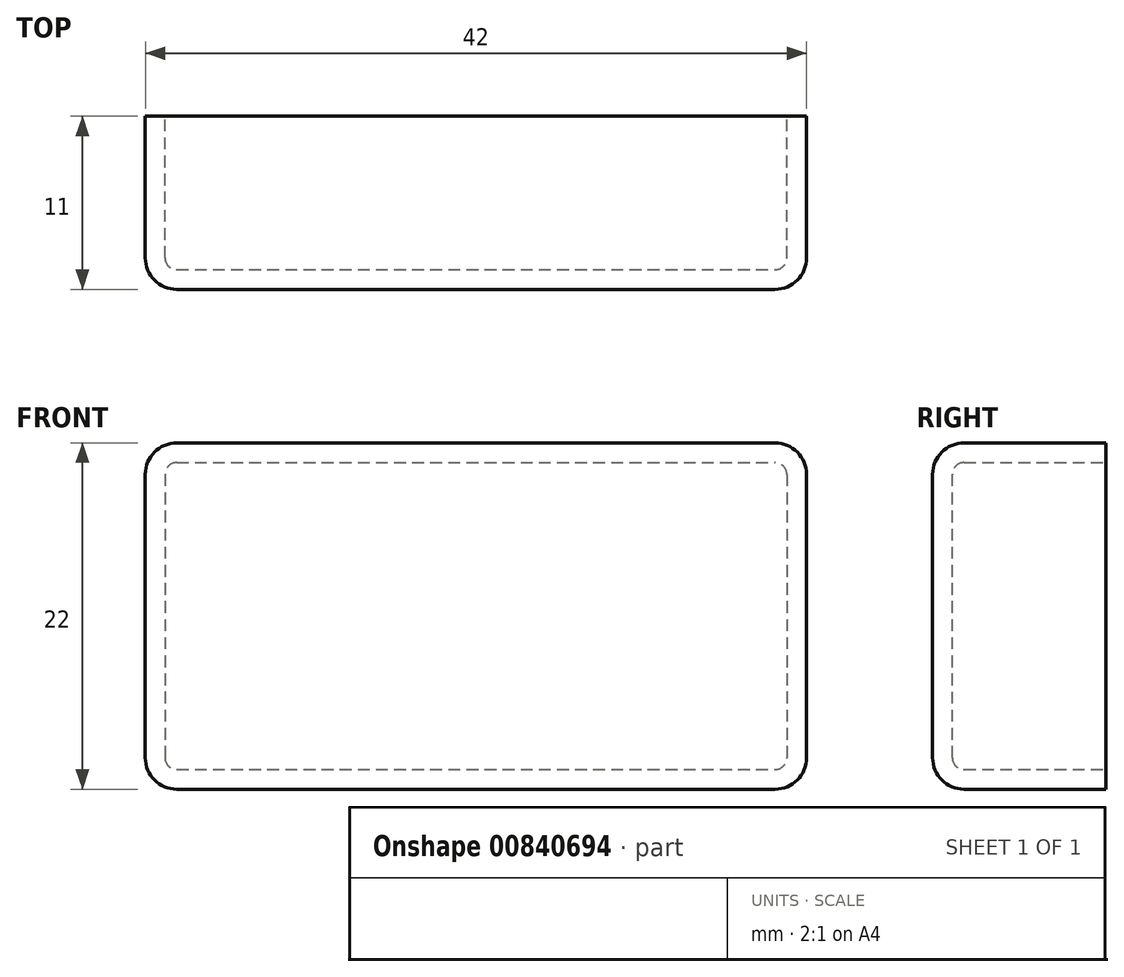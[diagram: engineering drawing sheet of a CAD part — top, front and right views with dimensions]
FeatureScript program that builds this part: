
annotation { "Feature Type Name" : "Feature", "Feature Type Description" : "" }
export const myFeature = defineFeature(function(context is Context, id is Id, definition is map)
    precondition{}
    {
        {
            var Q0;
            Q0=qCreatedBy(makeId("Front.planeOp"),FACE);
            var sketch = newSketch(context, id + "F0", { "sketchPlane" : qUnion([Q0])});
            skLineSegment(sketch, "E0.bottom", {"start": v(-16.62, 8.33) * mm, "end": v(25.38, 8.33) * mm});
            skLineSegment(sketch, "E0.top", {"start": v(-16.62, -13.67) * mm, "end": v(25.38, -13.67) * mm});
            skLineSegment(sketch, "E0.left", {"start": v(-16.62, 8.33) * mm, "end": v(-16.62, -13.67) * mm});
            skLineSegment(sketch, "E0.right", {"start": v(25.38, 8.33) * mm, "end": v(25.38, -13.67) * mm});
            skSolve(sketch);
        }
        {
            var Q0;
            Q0=makeQuery(id+"F0.imprint","IMPRINT",FACE,{"disambiguationData":[TD([[makeQuery(id+"F0.imprint","IMPRINT",EDGE,{"derivedFrom":sQuery(id+"F0.wireOp",EDGE,"E0.bottom")}),-1.0]])]});
            extrude(context, id + "F1", {"entities" : qUnion([Q0]), "depth" : 11 * mm, "offsetDistance" : 25 * mm});
        }
        {
            var Q0;
            Q0=makeQuery(id+"F1.opExtrude","SWEPT_EDGE",EDGE,{"disambiguationData":[OSD([sQuery(id+"F0.wireOp",EDGE,"E0.bottom"),sQuery(id+"F0.wireOp",EDGE,"E0.right")])]});
            var Q1;
            Q1=makeQuery(id+"F1.opExtrude","SWEPT_EDGE",EDGE,{"disambiguationData":[OSD([sQuery(id+"F0.wireOp",EDGE,"E0.top"),sQuery(id+"F0.wireOp",EDGE,"E0.right")])]});
            var Q2;
            Q2=makeQuery(id+"F1.opExtrude","SWEPT_EDGE",EDGE,{"disambiguationData":[OSD([sQuery(id+"F0.wireOp",EDGE,"E0.bottom"),sQuery(id+"F0.wireOp",EDGE,"E0.left")])]});
            var Q3;
            Q3=makeQuery(id+"F1.opExtrude","SWEPT_EDGE",EDGE,{"disambiguationData":[OSD([sQuery(id+"F0.wireOp",EDGE,"E0.top"),sQuery(id+"F0.wireOp",EDGE,"E0.left")])]});
            var Q4;
            Q4=makeQuery(id+"F1.opExtrude","CAP_EDGE",EDGE,{"disambiguationData":[OSD([sQuery(id+"F0.wireOp",EDGE,"E0.top")])],"isStart":false});
            var Q5;
            Q5=makeQuery(id+"F1.opExtrude","CAP_EDGE",EDGE,{"disambiguationData":[OSD([sQuery(id+"F0.wireOp",EDGE,"E0.right")])],"isStart":false});
            var Q6;
            Q6=makeQuery(id+"F1.opExtrude","CAP_EDGE",EDGE,{"disambiguationData":[OSD([sQuery(id+"F0.wireOp",EDGE,"E0.bottom")])],"isStart":false});
            var Q7;
            Q7=makeQuery(id+"F1.opExtrude","CAP_EDGE",EDGE,{"disambiguationData":[OSD([sQuery(id+"F0.wireOp",EDGE,"E0.left")])],"isStart":false});
            fillet(context, id + "F2", {"entities" : qUnion([Q0, Q1, Q2, Q3, Q4, Q5, Q6, Q7]), "radius" : 2 * mm, "tangentPropagation" : true, "allowEdgeOverflow" : false});
        }
        {
            var Q0;
            Q0=makeQuery(id+"F1.opExtrude","CAP_FACE",FACE,{"disambiguationData":[OSD([sQuery(id+"F0.wireOp",EDGE,"E0.bottom"),sQuery(id+"F0.wireOp",EDGE,"E0.top"),sQuery(id+"F0.wireOp",EDGE,"E0.left"),sQuery(id+"F0.wireOp",EDGE,"E0.right")])],"isStart":true});
            shell(context, id + "F3", {"entities" : qUnion([Q0]), "thickness" : 1.25 * mm});
        }
    });
